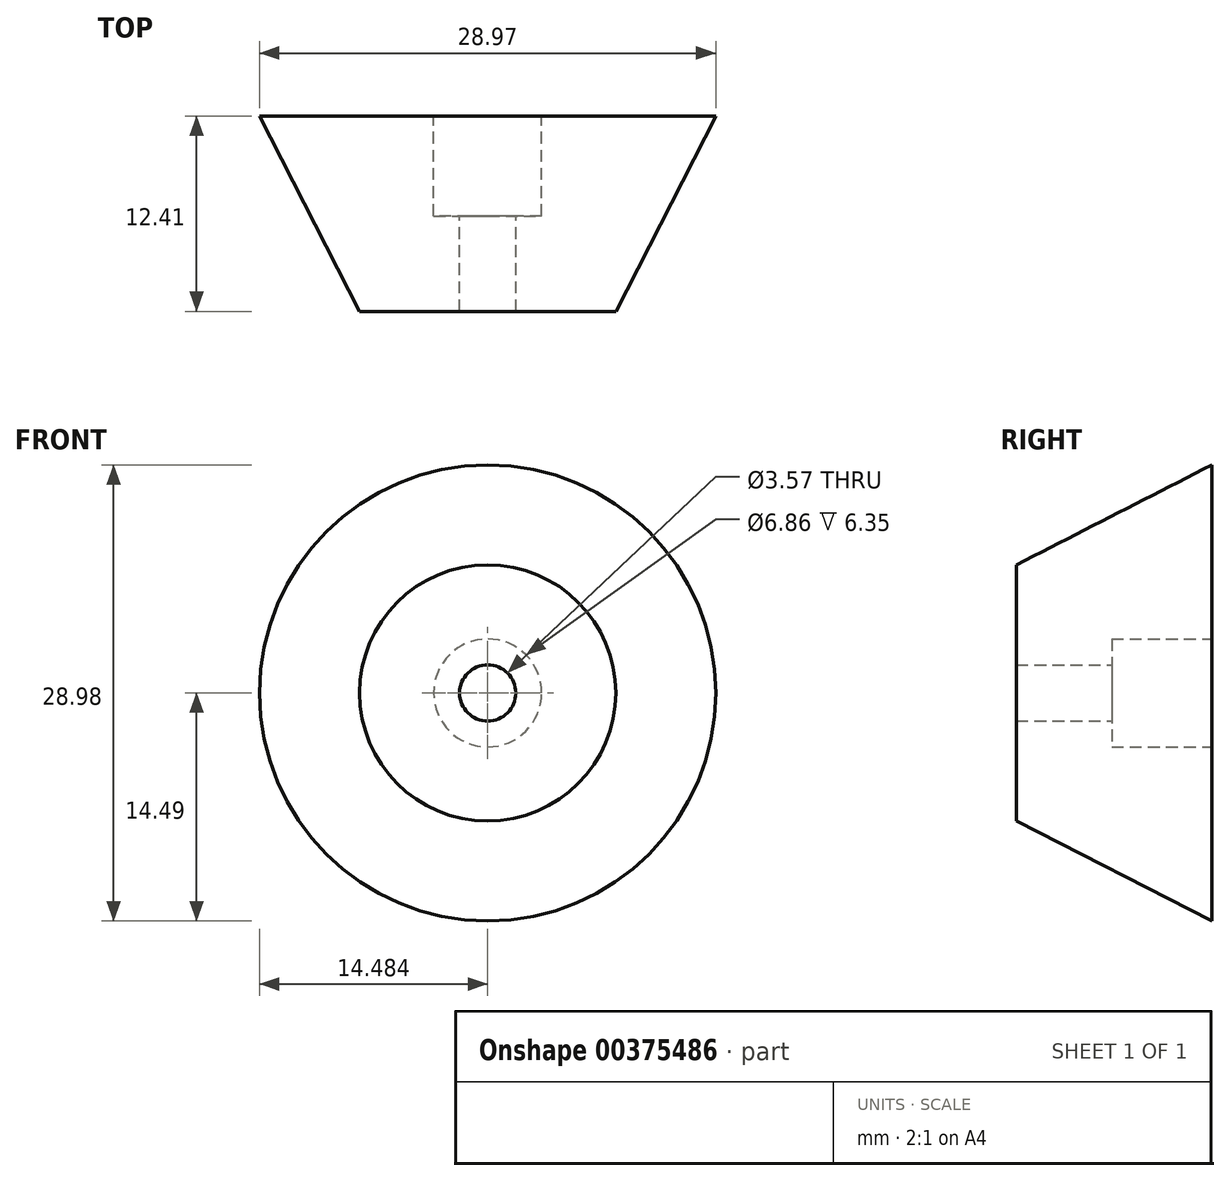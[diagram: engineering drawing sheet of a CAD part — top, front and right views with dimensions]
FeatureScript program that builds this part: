
annotation { "Feature Type Name" : "Feature", "Feature Type Description" : "" }
export const myFeature = defineFeature(function(context is Context, id is Id, definition is map)
    precondition{}
    {
        {
            var Q0;
            Q0=qCreatedBy(makeId("Top.planeOp"),FACE);
            var sketch = newSketch(context, id + "F0", { "sketchPlane" : qUnion([Q0])});
            skLineSegment(sketch, "E0", {"start": v(-8.14, -2.25) * mm, "end": v(-8.14, -14.95) * mm});
            skLineSegment(sketch, "E1", {"start": v(-6.35, -14.66) * mm, "end": v(0, -14.66) * mm});
            skLineSegment(sketch, "E2", {"start": v(-6.35, -2.25) * mm, "end": v(6.35, -2.25) * mm});
            skLineSegment(sketch, "E3", {"start": v(6.35, -2.25) * mm, "end": v(0, -14.66) * mm});
            skLineSegment(sketch, "E4", {"start": v(-6.35, -2.25) * mm, "end": v(-6.35, -14.66) * mm});
            skSolve(sketch);
        }
        {
            var Q0;
            Q0 = qSketchRegion(id + "F0", true);
            var Q1;
            Q1=sQuery(id+"F0.wireOp",EDGE,"E0");
            revolve(context, id + "F1", {"entities" : qUnion([Q0]), "axis" : qUnion([Q1]), "revolveType" : RevolveType.FULL});
        }
        {
            var Q0;
            Q0=makeQuery(id+"F1.opRevolve","SWEPT_FACE",FACE,{"disambiguationData":[OSD([sQuery(id+"F0.wireOp",EDGE,"E2")])]});
            var sketch = newSketch(context, id + "F2", { "sketchPlane" : qUnion([Q0])});
            skCircle(sketch, "E5", {"center": v(8.14, 0) * mm, "radius": 3.43 * mm});
            skSolve(sketch);
        }
        {
            var Q0;
            Q0 = qSketchRegion(id + "F2", true);
            extrude(context, id + "F3", {"entities" : qUnion([Q0]), "operationType" : NewBodyOperationType.REMOVE, "oppositeDirection" : true, "depth" : 6.35 * mm});
        }
    });
